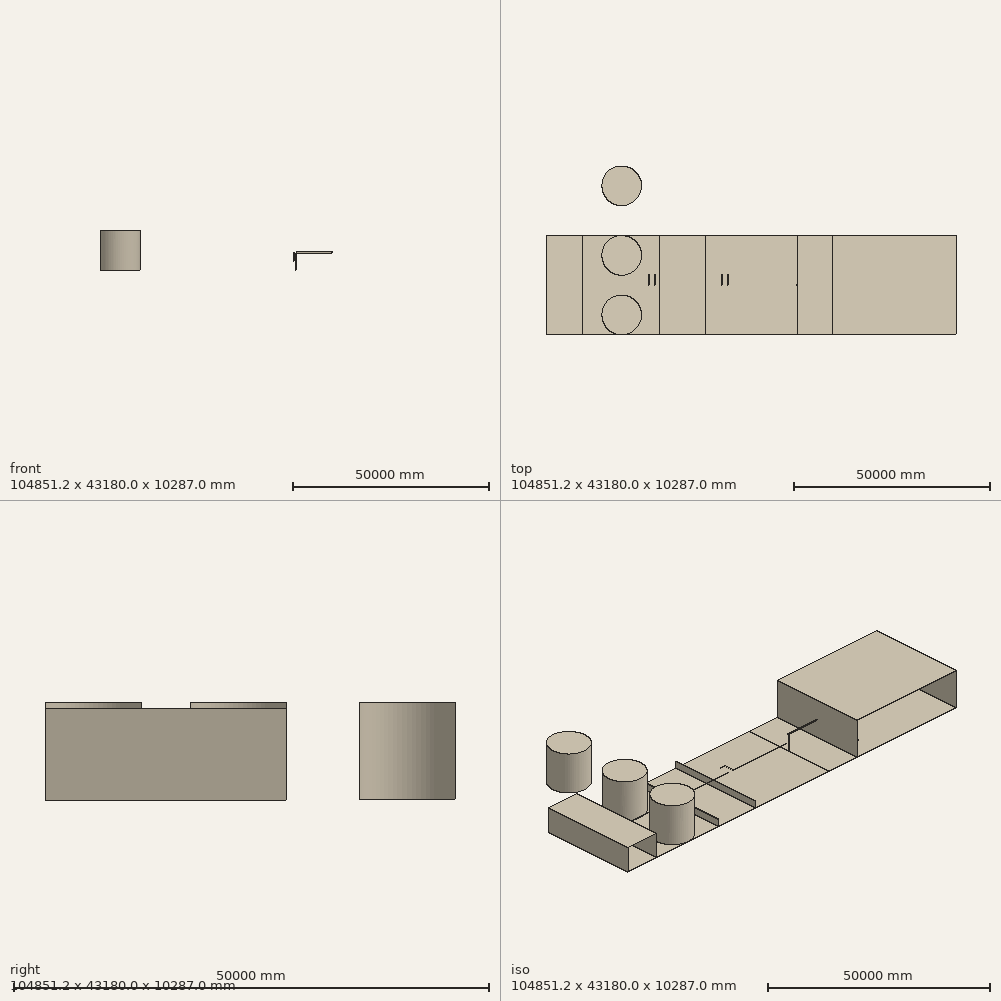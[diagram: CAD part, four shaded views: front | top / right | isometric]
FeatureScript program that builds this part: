
annotation { "Feature Type Name" : "Feature", "Feature Type Description" : "" }
export const myFeature = defineFeature(function(context is Context, id is Id, definition is map)
    precondition{}
    {
        {
            var Q0;
            Q0=qCreatedBy(makeId("Top.planeOp"),FACE);
            cPlane(context, id + "F0", {"entities" : qUnion([Q0]), "cplaneType" : CPlaneType.OFFSET, "offset" : 25.4 * mm, "width" : 152.4 * mm, "height" : 152.4 * mm});
        }
        {
            var Q0;
            Q0=qCreatedBy(id+"F0.planeOp",FACE);
            var sketch = newSketch(context, id + "F1", { "sketchPlane" : qUnion([Q0])});
            skLineSegment(sketch, "E0", {"start": v(0, 0) * mm, "end": v(9144, 0) * mm});
            skLineSegment(sketch, "E1", {"start": v(9144, 0) * mm, "end": v(24688.8, 0) * mm});
            skPoint(sketch, "E2.visualSharp", {"position": v(9144, 0) * mm});
            skSolve(sketch);
        }
        {
            var Q0;
            Q0=qCreatedBy(makeId("Front.planeOp"),FACE);
            var sketch = newSketch(context, id + "F2", { "sketchPlane" : qUnion([Q0])});
            skArc(sketch, "E3", {"start": v(0, 25.4) * mm, "mid": v(-80.82, -8.08) * mm, "end": v(-114.3, -88.9) * mm});
            skLineSegment(sketch, "E4", {"start": v(-114.3, -88.9) * mm, "end": v(-114.3, -2298.7) * mm});
            skArc(sketch, "E5", {"start": v(-228.6, -2413) * mm, "mid": v(-147.78, -2379.52) * mm, "end": v(-114.3, -2298.7) * mm});
            skLineSegment(sketch, "E6", {"start": v(-228.6, -2298.7) * mm, "end": v(-228.6, -2413) * mm, "construction": true});
            skSolve(sketch);
        }
        {
            var Q0;
            Q0=qCreatedBy(makeId("Top.planeOp"),FACE);
            var Q1;
            Q1=sQuery(id+"F2.wireOp",VERTEX,"E5.start");
            cPlane(context, id + "F3", {"entities" : qUnion([Q0, Q1]), "cplaneType" : CPlaneType.PLANE_POINT, "offset" : 25.4 * mm, "width" : 152.4 * mm, "height" : 152.4 * mm});
        }
        {
            var Q0;
            Q0=qCreatedBy(id+"F3.planeOp",FACE);
            var sketch = newSketch(context, id + "F4", { "sketchPlane" : qUnion([Q0])});
            skLineSegment(sketch, "E7", {"start": v(-228.6, 0) * mm, "end": v(-17170.4, 0) * mm});
            skLineSegment(sketch, "E8", {"start": v(-18808.7, 114.3) * mm, "end": v(-18808.7, 2628.9) * mm});
            skLineSegment(sketch, "E9", {"start": v(-17399, 2743.2) * mm, "end": v(-18694.4, 2743.2) * mm});
            skLineSegment(sketch, "E10", {"start": v(-17284.7, 2628.9) * mm, "end": v(-17284.7, 114.3) * mm});
            skLineSegment(sketch, "E11", {"start": v(-18923, 0) * mm, "end": v(-35864.8, 0) * mm});
            skLineSegment(sketch, "E12", {"start": v(-37503.1, 114.3) * mm, "end": v(-37503.1, 2628.9) * mm});
            skLineSegment(sketch, "E13", {"start": v(-36093.4, 2743.2) * mm, "end": v(-37388.8, 2743.2) * mm});
            skLineSegment(sketch, "E14", {"start": v(-35979.1, 2628.9) * mm, "end": v(-35979.1, 114.3) * mm});
            skLineSegment(sketch, "E15", {"start": v(-37617.4, 0) * mm, "end": v(-54559.2, 0) * mm});
            skPoint(sketch, "E16.visualSharp", {"position": v(-37503.1, 0) * mm});
            skArc(sketch, "E16.filletArc", {"start": v(-37617.4, 0) * mm, "mid": v(-37536.58, 33.48) * mm, "end": v(-37503.1, 114.3) * mm});
            skPoint(sketch, "E17.visualSharp", {"position": v(-37503.1, 2743.2) * mm});
            skArc(sketch, "E17.filletArc", {"start": v(-37388.8, 2743.2) * mm, "mid": v(-37469.62, 2709.72) * mm, "end": v(-37503.1, 2628.9) * mm});
            skPoint(sketch, "E18.visualSharp", {"position": v(-35979.1, 2743.2) * mm});
            skArc(sketch, "E18.filletArc", {"start": v(-35979.1, 2628.9) * mm, "mid": v(-36012.58, 2709.72) * mm, "end": v(-36093.4, 2743.2) * mm});
            skPoint(sketch, "E19.visualSharp", {"position": v(-35979.1, 0) * mm});
            skArc(sketch, "E19.filletArc", {"start": v(-35979.1, 114.3) * mm, "mid": v(-35945.62, 33.48) * mm, "end": v(-35864.8, 0) * mm});
            skPoint(sketch, "E20.visualSharp", {"position": v(-18808.7, 0) * mm});
            skArc(sketch, "E20.filletArc", {"start": v(-18923, 0) * mm, "mid": v(-18842.18, 33.48) * mm, "end": v(-18808.7, 114.3) * mm});
            skPoint(sketch, "E21.visualSharp", {"position": v(-18808.7, 2743.2) * mm});
            skArc(sketch, "E21.filletArc", {"start": v(-18694.4, 2743.2) * mm, "mid": v(-18775.22, 2709.72) * mm, "end": v(-18808.7, 2628.9) * mm});
            skPoint(sketch, "E22.visualSharp", {"position": v(-17284.7, 2743.2) * mm});
            skArc(sketch, "E22.filletArc", {"start": v(-17284.7, 2628.9) * mm, "mid": v(-17318.18, 2709.72) * mm, "end": v(-17399, 2743.2) * mm});
            skPoint(sketch, "E23.visualSharp", {"position": v(-17284.7, 0) * mm});
            skArc(sketch, "E23.filletArc", {"start": v(-17284.7, 114.3) * mm, "mid": v(-17251.22, 33.48) * mm, "end": v(-17170.4, 0) * mm});
            skSolve(sketch);
        }
        {
            var Q0;
            Q0=qCreatedBy(makeId("Right.planeOp"),FACE);
            var Q1;
            Q1=sQuery(id+"F1.wireOp",VERTEX,"E1.end");
            cPlane(context, id + "F5", {"entities" : qUnion([Q0, Q1]), "cplaneType" : CPlaneType.PLANE_POINT, "offset" : 25.4 * mm, "width" : 152.4 * mm, "height" : 152.4 * mm});
        }
        {
            var Q0;
            Q0=qCreatedBy(id+"F5.planeOp",FACE);
            var sketch = newSketch(context, id + "F6", { "sketchPlane" : qUnion([Q0])});
            skCircle(sketch, "E24", {"center": v(0, 25.4) * mm, "radius": 41.4 * mm});
            skCircle(sketch, "E25", {"center": v(0, 25.4) * mm, "radius": 44.45 * mm});
            skSolve(sketch);
        }
        {
            var Q0;
            Q0 = qSketchRegion(id + "F6", true);
            var Q1;
            Q1 = qConstructionFilter(qBodyType(qCreatedBy(id + "F4" ,EDGE), BodyType.WIRE), ConstructionObject.NO);
            var Q2;
            Q2 = qConstructionFilter(qBodyType(qCreatedBy(id + "F2" ,EDGE), BodyType.WIRE), ConstructionObject.NO);
            var Q3;
            Q3 = qConstructionFilter(qBodyType(qCreatedBy(id + "F1" ,EDGE), BodyType.WIRE), ConstructionObject.NO);
            sweep(context, id + "F7", {"profiles" : qUnion([Q0]), "path" : qUnion([Q1, Q2, Q3])});
        }
        {
            var Q0;
            Q0=qCreatedBy(makeId("Front.planeOp"),FACE);
            var sketch = newSketch(context, id + "F8", { "sketchPlane" : qUnion([Q0])});
            skLineSegment(sketch, "E26", {"start": v(-54559.2, -4673.6) * mm, "end": v(-34848.8, -4673.6) * mm});
            skLineSegment(sketch, "E27", {"start": v(457.2, -4673.6) * mm, "end": v(457.2, -4724.4) * mm});
            skLineSegment(sketch, "E28", {"start": v(457.2, -4724.4) * mm, "end": v(9448.8, -4724.4) * mm});
            skLineSegment(sketch, "E29", {"start": v(9448.8, -4724.4) * mm, "end": v(9448.8, 4876.8) * mm});
            skLineSegment(sketch, "E30", {"start": v(9448.8, 4876.8) * mm, "end": v(41148, 4876.8) * mm});
            skLineSegment(sketch, "E31", {"start": v(41148, 4876.8) * mm, "end": v(41148, -4800.6) * mm});
            skLineSegment(sketch, "E32", {"start": v(41148, -4800.6) * mm, "end": v(-54559.2, -4800.6) * mm});
            skLineSegment(sketch, "E33.top", {"start": v(-23114, -2844.8) * mm, "end": v(-23012.4, -2844.8) * mm});
            skLineSegment(sketch, "E33.left", {"start": v(-23114, -4673.6) * mm, "end": v(-23114, -2844.8) * mm});
            skLineSegment(sketch, "E33.right", {"start": v(-23012.4, -4673.6) * mm, "end": v(-23012.4, -2844.8) * mm});
            skLineSegment(sketch, "E34.trimOffspring", {"start": v(-23012.4, -4673.6) * mm, "end": v(457.2, -4673.6) * mm});
            skLineSegment(sketch, "E35.0", {"start": v(41097.2, -4749.8) * mm, "end": v(9499.6, -4749.8) * mm});
            skLineSegment(sketch, "E35.1", {"start": v(41097.2, 4826) * mm, "end": v(41097.2, -4749.8) * mm});
            skLineSegment(sketch, "E35.2", {"start": v(9499.6, 4826) * mm, "end": v(41097.2, 4826) * mm});
            skLineSegment(sketch, "E35.3", {"start": v(9499.6, -4749.8) * mm, "end": v(9499.6, 4826) * mm});
            skLineSegment(sketch, "E36", {"start": v(9734.42, -479.42) * mm, "end": v(9734.42, -323.85) * mm, "construction": true});
            skLineSegment(sketch, "E37", {"start": v(9734.42, -479.42) * mm, "end": v(9731.5, -479.42) * mm, "construction": true});
            skLineSegment(sketch, "E38", {"start": v(9734.42, -323.85) * mm, "end": v(9652, -323.85) * mm});
            skLineSegment(sketch, "E39", {"start": v(9652, -323.85) * mm, "end": v(9652, -329.7) * mm});
            skLineSegment(sketch, "E40", {"start": v(9652, -329.7) * mm, "end": v(9731.5, -329.7) * mm});
            skLineSegment(sketch, "E41", {"start": v(9731.5, -329.7) * mm, "end": v(9731.5, -479.42) * mm});
            skLineSegment(sketch, "E42.MirrorCS", {"start": v(9816.85, -323.85) * mm, "end": v(9816.85, -329.7) * mm});
            skLineSegment(sketch, "E43.MirrorCS", {"start": v(9734.42, -323.85) * mm, "end": v(9816.85, -323.85) * mm});
            skLineSegment(sketch, "E44.MirrorCS", {"start": v(9737.34, -329.7) * mm, "end": v(9737.34, -479.42) * mm});
            skLineSegment(sketch, "E45.MirrorCS", {"start": v(9816.85, -329.7) * mm, "end": v(9737.34, -329.7) * mm});
            skLineSegment(sketch, "E46.MirrorCS", {"start": v(9652, -629.16) * mm, "end": v(9731.5, -629.16) * mm});
            skLineSegment(sketch, "E47.MirrorCS", {"start": v(9731.5, -629.16) * mm, "end": v(9731.5, -479.42) * mm});
            skLineSegment(sketch, "E48.MirrorCS", {"start": v(9734.42, -635) * mm, "end": v(9816.85, -635) * mm});
            skLineSegment(sketch, "E49.MirrorCS", {"start": v(9737.34, -629.16) * mm, "end": v(9737.34, -479.42) * mm});
            skLineSegment(sketch, "E50.MirrorCS", {"start": v(9816.85, -635) * mm, "end": v(9816.85, -629.16) * mm});
            skLineSegment(sketch, "E51.MirrorCS", {"start": v(9816.85, -629.16) * mm, "end": v(9737.34, -629.16) * mm});
            skLineSegment(sketch, "E52.MirrorCS", {"start": v(9652, -635) * mm, "end": v(9652, -629.16) * mm});
            skLineSegment(sketch, "E53.MirrorCS", {"start": v(9734.42, -635) * mm, "end": v(9652, -635) * mm});
            skLineSegment(sketch, "E54", {"start": v(9731.5, -329.7) * mm, "end": v(9737.34, -329.7) * mm, "construction": true});
            skPoint(sketch, "E55", {"position": v(9734.42, -323.85) * mm});
            skLineSegment(sketch, "E56.bottom", {"start": v(-54559.2, -4800.6) * mm, "end": v(-63703.2, -4800.6) * mm});
            skLineSegment(sketch, "E56.top", {"start": v(-54559.2, 1549.4) * mm, "end": v(-63703.2, 1549.4) * mm});
            skLineSegment(sketch, "E56.left", {"start": v(-54559.2, -4673.6) * mm, "end": v(-54559.2, 1549.4) * mm});
            skLineSegment(sketch, "E56.right", {"start": v(-63703.2, -4800.6) * mm, "end": v(-63703.2, 1549.4) * mm});
            skLineSegment(sketch, "E57.top", {"start": v(-34848.8, -2844.8) * mm, "end": v(-34747.2, -2844.8) * mm});
            skLineSegment(sketch, "E57.left", {"start": v(-34848.8, -4673.6) * mm, "end": v(-34848.8, -2844.8) * mm});
            skLineSegment(sketch, "E57.right", {"start": v(-34747.2, -4673.6) * mm, "end": v(-34747.2, -2844.8) * mm});
            skLineSegment(sketch, "E58.trimOffspring", {"start": v(-34747.2, -4673.6) * mm, "end": v(-23114, -4673.6) * mm});
            skLineSegment(sketch, "E59.0", {"start": v(-54610, -4749.8) * mm, "end": v(-63652.4, -4749.8) * mm});
            skLineSegment(sketch, "E59.1", {"start": v(-63652.4, -4749.8) * mm, "end": v(-63652.4, 1498.6) * mm});
            skLineSegment(sketch, "E59.2", {"start": v(-54610, 1498.6) * mm, "end": v(-63652.4, 1498.6) * mm});
            skLineSegment(sketch, "E59.3", {"start": v(-54610, -4749.8) * mm, "end": v(-54610, 1498.6) * mm});
            skSolve(sketch);
        }
        {
            var Q0;
            Q0 = qSketchRegion(id + "F8", true);
            var Q1;
            Q1=makeQuery(id+"F8.imprint","IMPRINT",FACE,{"disambiguationData":[TD([[makeQuery(id+"F8.imprint","IMPRINT",EDGE,{"derivedFrom":sQuery(id+"F8.wireOp",EDGE,"E38")}),1.0]])]});
            extrude(context, id + "F9", {"entities" : qUnion([Q0, Q1]), "endBound" : BoundingType.SYMMETRIC, "depth" : 25400 * mm});
        }
        {
            var Q0;
            Q0=qCreatedBy(id+"F3.planeOp",FACE);
            cPlane(context, id + "F10", {"entities" : qUnion([Q0]), "cplaneType" : CPlaneType.OFFSET, "offset" : 2032 * mm, "oppositeDirection" : true, "width" : 152.4 * mm, "height" : 152.4 * mm});
        }
        {
            var Q0;
            Q0=qCreatedBy(id+"F10.planeOp",FACE);
            var sketch = newSketch(context, id + "F11", { "sketchPlane" : qUnion([Q0])});
            skLineSegment(sketch, "E60", {"start": v(0, 0) * mm, "end": v(-1732.5, 0) * mm, "construction": true});
            skCircle(sketch, "E61", {"center": v(9593.92, 0) * mm, "radius": 273.4 * mm});
            skCircle(sketch, "E62.1.0.0", {"center": v(5021.92, 0) * mm, "radius": 273.4 * mm});
            skCircle(sketch, "E62.2.0.0", {"center": v(449.92, 0) * mm, "radius": 273.4 * mm});
            skCircle(sketch, "E62.3.0.0", {"center": v(-4122.08, 0) * mm, "radius": 273.4 * mm});
            skCircle(sketch, "E62.4.0.0", {"center": v(-8694.08, 0) * mm, "radius": 273.4 * mm});
            skCircle(sketch, "E62.5.0.0", {"center": v(-13266.08, 0) * mm, "radius": 273.4 * mm});
            skCircle(sketch, "E62.6.0.0", {"center": v(-17838.08, 0) * mm, "radius": 273.4 * mm});
            skCircle(sketch, "E62.7.0.0", {"center": v(-22410.08, 0) * mm, "radius": 273.4 * mm});
            skCircle(sketch, "E62.8.0.0", {"center": v(-26982.08, 0) * mm, "radius": 273.4 * mm});
            skCircle(sketch, "E62.9.0.0", {"center": v(-31554.08, 0) * mm, "radius": 273.4 * mm});
            skCircle(sketch, "E62.10.0.0", {"center": v(-36126.08, 0) * mm, "radius": 273.4 * mm});
            skCircle(sketch, "E62.11.0.0", {"center": v(-40698.08, 0) * mm, "radius": 273.4 * mm});
            skLineSegment(sketch, "E62.direction1", {"start": v(9593.92, 0) * mm, "end": v(5021.92, 0) * mm, "construction": true});
            skSolve(sketch);
        }
        {
            var Q0;
            Q0=makeQuery(id+"F9.opExtrude","SWEPT_FACE",FACE,{"disambiguationData":[OSD([sQuery(id+"F8.wireOp",EDGE,"E26")])]});
            var sketch = newSketch(context, id + "F12", { "sketchPlane" : qUnion([Q0])});
            skCircle(sketch, "E63", {"center": v(-44450, 7620) * mm, "radius": 5080 * mm});
            skCircle(sketch, "E64", {"center": v(-44450, -7620) * mm, "radius": 5080 * mm});
            skCircle(sketch, "E65", {"center": v(-44450, 25400) * mm, "radius": 5080 * mm});
            skLineSegment(sketch, "E66", {"start": v(-44450, 25400) * mm, "end": v(-44450, 7620) * mm, "construction": true});
            skLineSegment(sketch, "E67", {"start": v(-44450, -7620) * mm, "end": v(-44450, 7620) * mm, "construction": true});
            skLineSegment(sketch, "E68", {"start": v(-44450, 0) * mm, "end": v(0, 0) * mm, "construction": true});
            skSolve(sketch);
        }
        {
            var Q0;
            Q0 = qSketchRegion(id + "F12", true);
            extrude(context, id + "F13", {"entities" : qUnion([Q0]), "operationType" : NewBodyOperationType.ADD, "depth" : 10160 * mm});
        }
        {
            var Q0;
            Q0=makeQuery(id+"F9.opExtrude","SWEPT_FACE",FACE,{"disambiguationData":[OSD([sQuery(id+"F8.wireOp",EDGE,"E42.MirrorCS")])]});
            var sketch = newSketch(context, id + "F14", { "sketchPlane" : qUnion([Q0])});
            skLineSegment(sketch, "E69.bottom", {"start": v(-50.8, -323.85) * mm, "end": v(50.8, -323.85) * mm});
            skLineSegment(sketch, "E69.top", {"start": v(-50.8, -19.05) * mm, "end": v(50.8, -19.05) * mm});
            skLineSegment(sketch, "E69.left", {"start": v(-50.8, -323.85) * mm, "end": v(-50.8, -19.05) * mm});
            skLineSegment(sketch, "E69.right", {"start": v(50.8, -323.85) * mm, "end": v(50.8, -317.5) * mm});
            skLineSegment(sketch, "E70.bottom", {"start": v(50.8, -25.4) * mm, "end": v(-44.45, -25.4) * mm});
            skLineSegment(sketch, "E70.top", {"start": v(50.8, -317.5) * mm, "end": v(-44.45, -317.5) * mm});
            skLineSegment(sketch, "E70.right", {"start": v(-44.45, -25.4) * mm, "end": v(-44.45, -317.5) * mm});
            skLineSegment(sketch, "E71.trimOffspring", {"start": v(50.8, -25.4) * mm, "end": v(50.8, -19.05) * mm});
            skLineSegment(sketch, "E72", {"start": v(-50.8, -171.45) * mm, "end": v(-44.45, -171.45) * mm, "construction": true});
            skLineSegment(sketch, "E73", {"start": v(0, -19.05) * mm, "end": v(0, 25.4) * mm, "construction": true});
            skCircle(sketch, "E74.0", {"center": v(0, 25.4) * mm, "radius": 44.45 * mm, "construction": true});
            skSolve(sketch);
        }
        {
            var Q0;
            Q0 = qSketchRegion(id + "F14", true);
            extrude(context, id + "F15", {"entities" : qUnion([Q0]), "oppositeDirection" : true, "depth" : 9448.8 * mm});
        }
        {
            var Q0;
            Q0=makeQuery(id+"F15.opExtrude","SWEPT_FACE",FACE,{"disambiguationData":[OSD([sQuery(id+"F14.wireOp",EDGE,"E69.bottom")])]});
            var sketch = newSketch(context, id + "F16", { "sketchPlane" : qUnion([Q0])});
            skLineSegment(sketch, "E75", {"start": v(368.05, 0) * mm, "end": v(368.05, 152.4) * mm, "construction": true});
            skLineSegment(sketch, "E76", {"start": v(368.05, 0) * mm, "end": v(361.14, 0) * mm, "construction": true});
            skLineSegment(sketch, "E77", {"start": v(368.05, 152.4) * mm, "end": v(285.5, 152.4) * mm});
            skLineSegment(sketch, "E78", {"start": v(285.5, 152.4) * mm, "end": v(285.5, 138.58) * mm});
            skLineSegment(sketch, "E79", {"start": v(285.5, 138.58) * mm, "end": v(361.14, 138.58) * mm});
            skLineSegment(sketch, "E80", {"start": v(361.14, 138.58) * mm, "end": v(361.14, 0) * mm});
            skLineSegment(sketch, "E81.MirrorCS", {"start": v(450.6, 152.4) * mm, "end": v(450.6, 138.58) * mm});
            skLineSegment(sketch, "E82.MirrorCS", {"start": v(368.05, 152.4) * mm, "end": v(450.6, 152.4) * mm});
            skLineSegment(sketch, "E83.MirrorCS", {"start": v(374.95, 138.58) * mm, "end": v(374.95, 0) * mm});
            skLineSegment(sketch, "E84.MirrorCS", {"start": v(450.6, 138.58) * mm, "end": v(374.95, 138.58) * mm});
            skLineSegment(sketch, "E85.MirrorCS", {"start": v(285.5, -138.58) * mm, "end": v(361.14, -138.58) * mm});
            skLineSegment(sketch, "E86.MirrorCS", {"start": v(361.14, -138.58) * mm, "end": v(361.14, 0) * mm});
            skLineSegment(sketch, "E87.MirrorCS", {"start": v(368.05, -152.4) * mm, "end": v(450.6, -152.4) * mm});
            skLineSegment(sketch, "E88.MirrorCS", {"start": v(374.95, -138.58) * mm, "end": v(374.95, 0) * mm});
            skLineSegment(sketch, "E89.MirrorCS", {"start": v(450.6, -152.4) * mm, "end": v(450.6, -138.58) * mm});
            skLineSegment(sketch, "E90.MirrorCS", {"start": v(450.6, -138.58) * mm, "end": v(374.95, -138.58) * mm});
            skLineSegment(sketch, "E91.MirrorCS", {"start": v(285.5, -152.4) * mm, "end": v(285.5, -138.58) * mm});
            skLineSegment(sketch, "E92.MirrorCS", {"start": v(368.05, -152.4) * mm, "end": v(285.5, -152.4) * mm});
            skLineSegment(sketch, "E93", {"start": v(361.14, 138.58) * mm, "end": v(374.95, 138.58) * mm, "construction": true});
            skLineSegment(sketch, "E94", {"start": v(368.05, 152.4) * mm, "end": v(368.05, 152.4) * mm});
            skSolve(sketch);
        }
        {
            var Q0;
            Q0 = qSketchRegion(id + "F16", true);
            var Q1;
            Q1=makeQuery(id+"F9.opExtrude","SWEPT_FACE",FACE,{"disambiguationData":[OSD([sQuery(id+"F8.wireOp",EDGE,"E34.trimOffspring")])]});
            extrude(context, id + "F17", {"entities" : qUnion([Q0]), "operationType" : NewBodyOperationType.ADD, "endBound" : BoundingType.UP_TO_SURFACE, "endBoundEntityFace" : qUnion([Q1]), "depth" : 25.4 * mm});
        }
        {
            var Q0;
            Q0=qCreatedBy(makeId("Front.planeOp"),FACE);
            var sketch = newSketch(context, id + "F18", { "sketchPlane" : qUnion([Q0])});
            skLineSegment(sketch, "E95.bottom", {"start": v(285.5, -323.85) * mm, "end": v(450.6, -323.85) * mm});
            skLineSegment(sketch, "E95.top", {"start": v(285.5, -330.2) * mm, "end": v(450.6, -330.2) * mm});
            skLineSegment(sketch, "E95.left", {"start": v(285.5, -323.85) * mm, "end": v(285.5, -330.2) * mm});
            skLineSegment(sketch, "E95.right", {"start": v(450.6, -323.85) * mm, "end": v(450.6, -330.2) * mm});
            skLineSegment(sketch, "E96.bottom", {"start": v(285.5, -3625.85) * mm, "end": v(450.6, -3625.85) * mm});
            skLineSegment(sketch, "E96.top", {"start": v(285.5, -3632.2) * mm, "end": v(450.6, -3632.2) * mm});
            skLineSegment(sketch, "E96.left", {"start": v(285.5, -3625.85) * mm, "end": v(285.5, -3632.2) * mm});
            skLineSegment(sketch, "E96.right", {"start": v(450.6, -3625.85) * mm, "end": v(450.6, -3632.2) * mm});
            skSolve(sketch);
        }
        {
            var Q0;
            Q0 = qSketchRegion(id + "F18", true);
            var Q1;
            Q1=makeQuery(id+"F17.opExtrude","SWEPT_FACE",FACE,{"disambiguationData":[OSD([sQuery(id+"F16.wireOp",EDGE,"E77"),sQuery(id+"F16.wireOp",EDGE,"E82.MirrorCS")])]});
            var Q2;
            Q2=makeQuery(id+"F17.opExtrude","SWEPT_FACE",FACE,{"disambiguationData":[OSD([sQuery(id+"F16.wireOp",EDGE,"E87.MirrorCS"),sQuery(id+"F16.wireOp",EDGE,"E92.MirrorCS")])]});
            extrude(context, id + "F19", {"entities" : qUnion([Q0]), "operationType" : NewBodyOperationType.ADD, "endBound" : BoundingType.UP_TO_SURFACE, "endBoundEntityFace" : qUnion([Q1]), "depth" : 25.4 * mm, "hasSecondDirection" : true, "secondDirectionBound" : SecondDirectionBoundingType.UP_TO_SURFACE, "secondDirectionOppositeDirection" : true, "secondDirectionBoundEntityFace" : qUnion([Q2]), "secondDirectionDepth" : 25.4 * mm});
        }
    });
